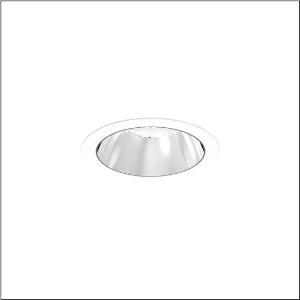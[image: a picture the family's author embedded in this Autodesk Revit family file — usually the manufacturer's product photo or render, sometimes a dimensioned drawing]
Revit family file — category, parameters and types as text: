
# Revit family: lunis_21_l_51db15ed91c
name_source: partatom
category: Lighting Fixtures
units: mm (PartAtom-declared; Revit-internal decimal feet)

## family parameters
Cut with Voids When Loaded = No
Host = Face
Light Source = No
Part Type = Normal
Room Calculation Point = No
Round Connector Dimension = Use Diameter
Shared = No

## types (1)
- --- (1 x LED, 4100 lm, 25.4 W, 4000K)
    Apparent Load = 25 VA
    CIE Flux Codes = 90 99 100 100 100
    Color Rendering = 80
    Color Temperature = 4000K
    Default Elevation = 1800 mm
    Description = Lunis 21,  L, downlight, light control with lens, of PMMA, anti glare with reflector, of PC, highly specular, light emission: direct distribution, LED rated luminous flux: 2.120lm, light colour: 830/840/865, with terminal, 5-pole, mains connection: 220..240V, AC/DC, 0/50..60Hz, housing, round, of diecast aluminium, traffic white (RAL 9016), diameter: 165mm, clamping range: 1..40mm, protection rating (complete): IP20, protection rating (on room side): IP54, insulation class (complete): insulation class II (safety insulation), certification: CE, impact resistance: IK03, packaging unit: 1 piece
    Height = 0 mm  [stored 0 ft]
    Lamp = 1 x LED
    Lamp Light Flux = 4100 lm
    Lamp Power = 25.4 W
    Lamp count = 1
    Length = 165 mm
    Luminous efficacy = 161 lm/W
    Manufacturer = Siteco
    ModVariant = No
    Model = 51DB15ED91C
    Mounting Place = Ceiling
    Mounting Type = Recessed
    Number of Poles = 1
    OnlyDefault = Yes
    Power Factor = 1
    Product Name = Lunis 21 L
    Product group = downlight
    ProductGroupID = 401
    Protection Class = Protection class II
    Protection Degree = IP 20
    RLX_Detail_Level = 1
    RLX_Emergency_Light_Flux = 0 lm
    RLX_Emergency_Type = 0
    RLX_Emergency_Type_DB = No
    RlxData = <blob elided: 14849 chars, md5=3c1bde58>
    Socket = socket
    Standby Power = 0 W
    System Light Flux = 4100 lm
    System Power = 25 W
    Type Comments = individual setting: colour temperature 4000K, luminous flux: 100 % | (ON | ON | OFF | OFF) | 700 mA
    Type Image = l_1291167.jpg
    URL = http://relux.com
    VarID = @adj_031627
    Voltage = 0 V
    Weight = 0.00 kg
    Width = 0 mm  [stored 0 ft]

note: [stored X ft] marks values corroborated as IEEE doubles in the binary element streams (Revit-internal decimal feet)

## geometry (parser evidence)
native form markers: Sweep x10
no freeform markers — native parametric forms only
